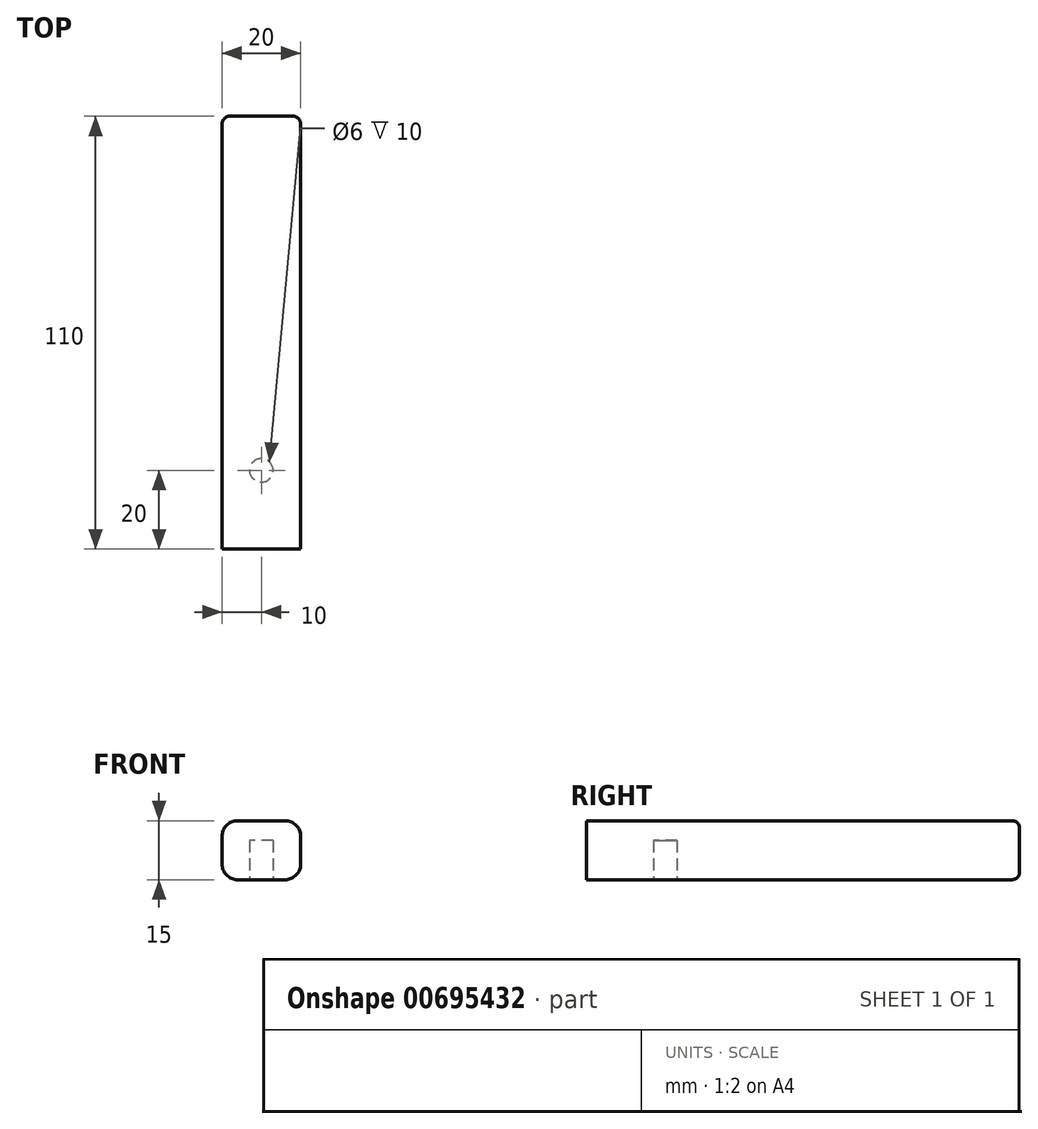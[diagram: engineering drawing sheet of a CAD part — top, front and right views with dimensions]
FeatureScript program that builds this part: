
annotation { "Feature Type Name" : "Feature", "Feature Type Description" : "" }
export const myFeature = defineFeature(function(context is Context, id is Id, definition is map)
    precondition{}
    {
        {
            var Q0;
            Q0=qCreatedBy(makeId("Top.planeOp"),FACE);
            var sketch = newSketch(context, id + "F0", { "sketchPlane" : qUnion([Q0])});
            skLineSegment(sketch, "E0.bottom", {"start": v(10, -20) * mm, "end": v(-10, -20) * mm});
            skLineSegment(sketch, "E0.top", {"start": v(10, 90) * mm, "end": v(-10, 90) * mm});
            skLineSegment(sketch, "E0.left", {"start": v(10, -20) * mm, "end": v(10, 90) * mm});
            skLineSegment(sketch, "E0.right", {"start": v(-10, -20) * mm, "end": v(-10, 90) * mm});
            skSolve(sketch);
        }
        {
            var Q0;
            Q0=makeQuery(id+"F0.imprint","IMPRINT",FACE,{"disambiguationData":[TD([[makeQuery(id+"F0.imprint","IMPRINT",EDGE,{"derivedFrom":sQuery(id+"F0.wireOp",EDGE,"E0.bottom")}),-1.0]])]});
            extrude(context, id + "F1", {"entities" : qUnion([Q0]), "depth" : 15 * mm, "offsetDistance" : 25 * mm});
        }
        {
            var Q0;
            Q0=qCreatedBy(makeId("Top.planeOp"),FACE);
            var sketch = newSketch(context, id + "F2", { "sketchPlane" : qUnion([Q0])});
            skCircle(sketch, "E1", {"center": v(0, 0) * mm, "radius": 3 * mm});
            skSolve(sketch);
        }
        {
            var Q0;
            Q0=makeQuery(id+"F2.imprint","IMPRINT",FACE,{"disambiguationData":[TD([[makeQuery(id+"F2.imprint","IMPRINT",EDGE,{"derivedFrom":sQuery(id+"F2.wireOp",EDGE,"E1")}),1.0]])]});
            var Q1;
            Q1=sQuery(id+"F2.wireOp",EDGE,"E1");
            extrude(context, id + "F3", {"entities" : qUnion([Q0]), "operationType" : NewBodyOperationType.REMOVE, "surfaceEntities" : qUnion([Q1]), "depth" : 10 * mm, "offsetDistance" : 25 * mm});
        }
        {
            var Q0;
            Q0=makeQuery(id+"F1.opExtrude","CAP_EDGE",EDGE,{"disambiguationData":[OSD([sQuery(id+"F0.wireOp",EDGE,"E0.left")])],"isStart":false});
            var Q1;
            Q1=makeQuery(id+"F1.opExtrude","CAP_EDGE",EDGE,{"disambiguationData":[OSD([sQuery(id+"F0.wireOp",EDGE,"E0.right")])],"isStart":false});
            var Q2;
            Q2=makeQuery(id+"F1.opExtrude","CAP_EDGE",EDGE,{"disambiguationData":[OSD([sQuery(id+"F0.wireOp",EDGE,"E0.left")])],"isStart":true});
            var Q3;
            Q3=makeQuery(id+"F1.opExtrude","CAP_EDGE",EDGE,{"disambiguationData":[OSD([sQuery(id+"F0.wireOp",EDGE,"E0.right")])],"isStart":true});
            fillet(context, id + "F4", {"entities" : qUnion([Q0, Q1, Q2, Q3]), "radius" : 4 * mm, "tangentPropagation" : true, "allowEdgeOverflow" : false});
        }
        {
            var Q0;
            Q0=makeQuery(id+"F4.opFillet","BLEND_EDGE",EDGE,{"blendedFrom":[makeQuery(id+"F1.opExtrude","CAP_EDGE",EDGE,{"disambiguationData":[OSD([sQuery(id+"F0.wireOp",EDGE,"E0.left")])],"isStart":true}),makeQuery(id+"F1.opExtrude","SWEPT_FACE",FACE,{"disambiguationData":[OSD([sQuery(id+"F0.wireOp",EDGE,"E0.top")])]})],"blendedInto":[makeQuery(id+"F1.opExtrude","SWEPT_FACE",FACE,{"disambiguationData":[OSD([sQuery(id+"F0.wireOp",EDGE,"E0.top")])]})]});
            fillet(context, id + "F5", {"entities" : qUnion([Q0]), "radius" : 2 * mm, "tangentPropagation" : true, "allowEdgeOverflow" : false});
        }
    });
